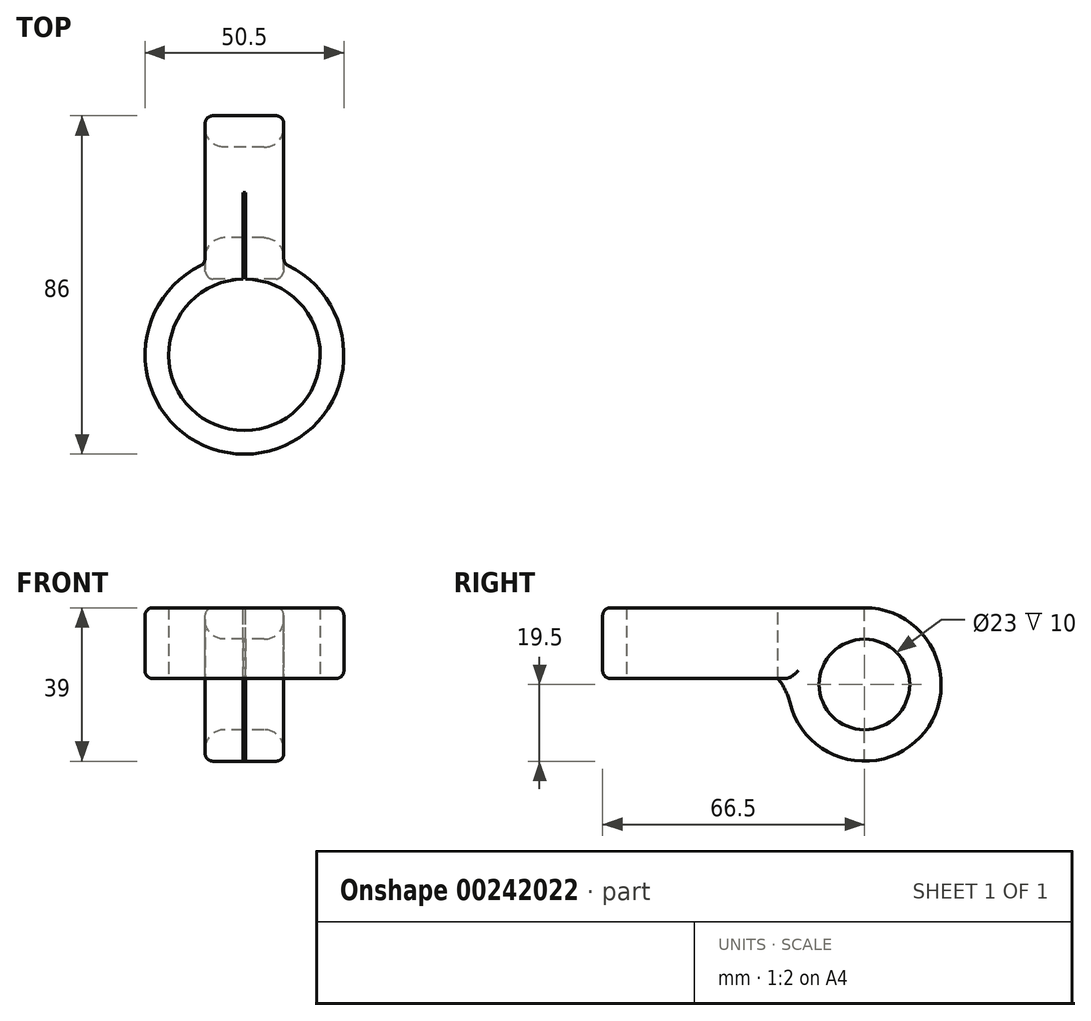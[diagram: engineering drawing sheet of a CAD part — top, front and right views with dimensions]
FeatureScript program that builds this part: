
annotation { "Feature Type Name" : "Feature", "Feature Type Description" : "" }
export const myFeature = defineFeature(function(context is Context, id is Id, definition is map)
    precondition{}
    {
        {
            var Q0;
            Q0=qCreatedBy(makeId("Top.planeOp"),FACE);
            var sketch = newSketch(context, id + "F0", { "sketchPlane" : qUnion([Q0])});
            skCircle(sketch, "E0", {"center": v(0, 0) * mm, "radius": 19.25 * mm});
            skCircle(sketch, "E1.0", {"center": v(0, 0) * mm, "radius": 25.25 * mm});
            skSolve(sketch);
        }
        {
            var Q0;
            Q0=makeQuery(id+"F0.imprint","IMPRINT",FACE,{"disambiguationData":[TD([[makeQuery(id+"F0.imprint","IMPRINT",EDGE,{"derivedFrom":sQuery(id+"F0.wireOp",EDGE,"E0")}),-1.0]])]});
            extrude(context, id + "F1", {"entities" : qUnion([Q0]), "depth" : 18 * mm});
        }
        {
            var Q0;
            Q0=qCreatedBy(makeId("Right.planeOp"),FACE);
            var sketch = newSketch(context, id + "F2", { "sketchPlane" : qUnion([Q0])});
            skLineSegment(sketch, "E2", {"start": v(19.25, 18) * mm, "end": v(19.25, 0) * mm});
            skCircle(sketch, "E3", {"center": v(41.25, -1.5) * mm, "radius": 11.5 * mm});
            skArc(sketch, "E4", {"start": v(22.3, -6.07) * mm, "mid": v(21.12, -2.86) * mm, "end": v(19.25, 0) * mm});
            skArc(sketch, "E5", {"start": v(41.25, 18) * mm, "mid": v(25.93, 10.57) * mm, "end": v(22.3, -6.07) * mm, "construction": true});
            skArc(sketch, "E6", {"start": v(22.3, -6.07) * mm, "mid": v(56.57, -13.57) * mm, "end": v(41.25, 18) * mm});
            skLineSegment(sketch, "E7", {"start": v(19.25, 18) * mm, "end": v(41.25, 18) * mm});
            skSolve(sketch);
        }
        {
            var Q0;
            Q0=makeQuery(id+"F2.imprint","IMPRINT",FACE,{"disambiguationData":[TD([[makeQuery(id+"F2.imprint","IMPRINT",EDGE,{"derivedFrom":sQuery(id+"F2.wireOp",EDGE,"E2")}),1.0]])]});
            extrude(context, id + "F3", {"entities" : qUnion([Q0]), "operationType" : NewBodyOperationType.ADD, "endBound" : BoundingType.SYMMETRIC, "depth" : 20 * mm});
        }
        {
            var Q0;
            Q0=makeQuery(id+"F3.opExtrude","CAP_EDGE",EDGE,{"disambiguationData":[OSD([sQuery(id+"F2.wireOp",EDGE,"E7")])],"isStart":true});
            var Q1;
            Q1=makeQuery(id+"F3.opExtrude","CAP_EDGE",EDGE,{"disambiguationData":[OSD([sQuery(id+"F2.wireOp",EDGE,"E7")])],"isStart":false});
            var Q2;
            Q2=makeQuery(id+"F1.opExtrude","CAP_EDGE",EDGE,{"disambiguationData":[OSD([sQuery(id+"F0.wireOp",EDGE,"E1.0")])],"isStart":false});
            var Q3;
            Q3=makeQuery(id+"F3.boolean.opBoolean","INTERSECT",EDGE,{"derivedFrom":[makeQuery(id+"F1.opExtrude","SWEPT_FACE",FACE,{"disambiguationData":[OSD([sQuery(id+"F0.wireOp",EDGE,"E1.0")])]}),makeQuery(id+"F3.opExtrude","CAP_FACE",FACE,{"disambiguationData":[OSD([sQuery(id+"F2.wireOp",EDGE,"E2"),sQuery(id+"F2.wireOp",EDGE,"E3"),sQuery(id+"F2.wireOp",EDGE,"E4"),sQuery(id+"F2.wireOp",EDGE,"E6"),sQuery(id+"F2.wireOp",EDGE,"E7")])],"isStart":false})]});
            var Q4;
            Q4=makeQuery(id+"F3.boolean.opBoolean","INTERSECT",EDGE,{"derivedFrom":[makeQuery(id+"F1.opExtrude","SWEPT_FACE",FACE,{"disambiguationData":[OSD([sQuery(id+"F0.wireOp",EDGE,"E1.0")])]}),makeQuery(id+"F3.opExtrude","CAP_FACE",FACE,{"disambiguationData":[OSD([sQuery(id+"F2.wireOp",EDGE,"E2"),sQuery(id+"F2.wireOp",EDGE,"E3"),sQuery(id+"F2.wireOp",EDGE,"E4"),sQuery(id+"F2.wireOp",EDGE,"E6"),sQuery(id+"F2.wireOp",EDGE,"E7")])],"isStart":true})]});
            fillet(context, id + "F4", {"entities" : qUnion([Q0, Q1, Q2, Q3, Q4]), "radius" : 2 * mm, "tangentPropagation" : true, "allowEdgeOverflow" : false});
        }
        {
            var Q0;
            Q0=makeQuery(id+"F3.opExtrude","SWEPT_FACE",FACE,{"disambiguationData":[OSD([sQuery(id+"F2.wireOp",EDGE,"E3")])]});
            fillet(context, id + "F5", {"entities" : qUnion([Q0]), "radius" : 5 * mm, "tangentPropagation" : true, "allowEdgeOverflow" : false});
        }
        {
            var Q0;
            Q0=makeQuery(id+"F3.boolean.opBoolean","MERGE",FACE,{"derivedFrom":[makeQuery(id+"F1.opExtrude","CAP_FACE",FACE,{"disambiguationData":[OSD([sQuery(id+"F0.wireOp",EDGE,"E0"),sQuery(id+"F0.wireOp",EDGE,"E1.0")])],"isStart":false}),makeQuery(id+"F3.opExtrude","SWEPT_FACE",FACE,{"disambiguationData":[OSD([sQuery(id+"F2.wireOp",EDGE,"E7")])]})]});
            var sketch = newSketch(context, id + "F6", { "sketchPlane" : qUnion([Q0])});
            skLineSegment(sketch, "E8.bottom", {"start": v(0.3, 0) * mm, "end": v(-0.3, 0) * mm});
            skLineSegment(sketch, "E8.top", {"start": v(0.3, 60.75) * mm, "end": v(-0.3, 60.75) * mm});
            skLineSegment(sketch, "E8.left", {"start": v(0.3, 0) * mm, "end": v(0.3, 60.75) * mm});
            skLineSegment(sketch, "E8.right", {"start": v(-0.3, 0) * mm, "end": v(-0.3, 60.75) * mm});
            skPoint(sketch, "E8.middle", {"position": v(0, 30.38) * mm});
            skLineSegment(sketch, "E9", {"start": v(-8, 60.75) * mm, "end": v(8, 60.75) * mm});
            skSolve(sketch);
        }
        {
            var Q0;
            {var subQ0=sQuery(id+"F6.wireOp",EDGE,"E9");var subQ1=sQuery(id+"F6.wireOp",EDGE,"E8.left");var subQ2=makeQuery(id+"F6.imprint","INTERSECT",VERTEX,{"derivedFrom":[subQ1,subQ0]});Q0=makeQuery(id+"F6.imprint","IMPRINT",FACE,{"disambiguationData":[TD([[makeQuery(id+"F6.imprint","IMPRINT",EDGE,{"disambiguationData":[TD([[subQ2,1.0]])],"derivedFrom":subQ0}),-1.0]])]});}
            var Q1;
            {var subQ0=sQuery(id+"F6.wireOp",EDGE,"E8.left");var subQ3=makeQuery(id+"F1.opExtrude","CAP_EDGE",EDGE,{"disambiguationData":[OSD([sQuery(id+"F0.wireOp",EDGE,"E0")])],"isStart":false});var subQ4=makeQuery(id+"F6.imprint","INTERSECT",VERTEX,{"derivedFrom":[subQ3,subQ0]});Q1=makeQuery(id+"F6.imprint","IMPRINT",FACE,{"disambiguationData":[TD([[makeQuery(id+"F6.imprint","IMPRINT",EDGE,{"disambiguationData":[TD([[subQ4,-1.0]])],"derivedFrom":subQ3}),-1.0]])]});}
            extrude(context, id + "F7", {"entities" : qUnion([Q0, Q1]), "operationType" : NewBodyOperationType.REMOVE, "endBound" : BoundingType.THROUGH_ALL, "oppositeDirection" : true, "depth" : 25 * mm});
        }
        {
            var Q0;
            Q0=makeQuery(id+"F1.opExtrude","CAP_EDGE",EDGE,{"disambiguationData":[OSD([sQuery(id+"F0.wireOp",EDGE,"E1.0")])],"isStart":true});
            fillet(context, id + "F8", {"entities" : qUnion([Q0]), "radius" : 2 * mm, "tangentPropagation" : true, "allowEdgeOverflow" : false});
        }
    });
